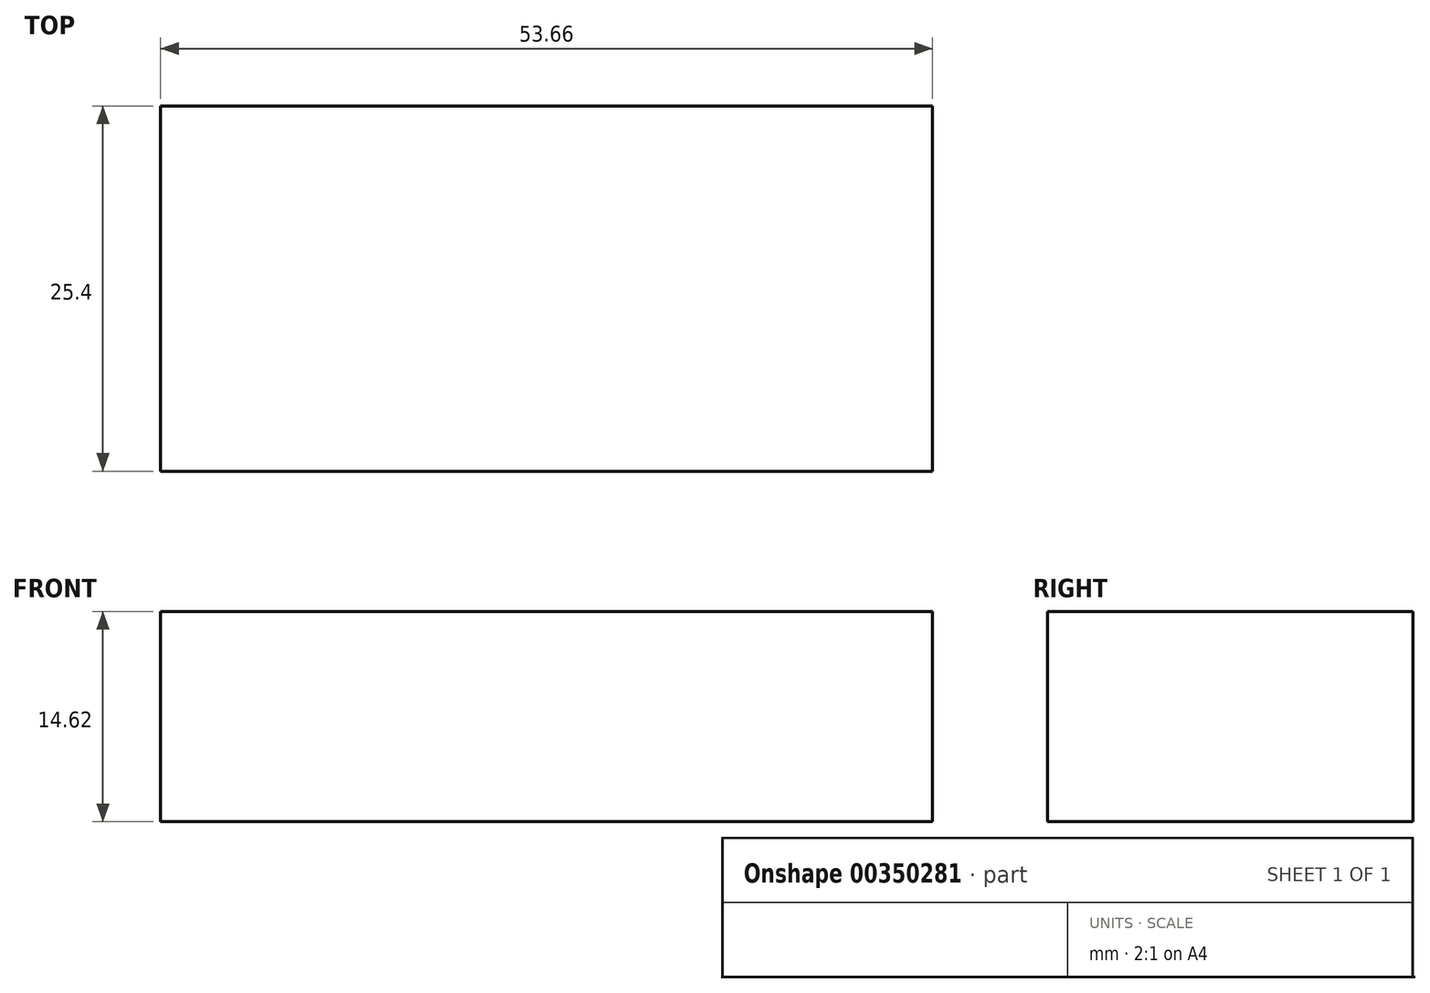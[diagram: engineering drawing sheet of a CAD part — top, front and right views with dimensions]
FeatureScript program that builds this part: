
annotation { "Feature Type Name" : "Feature", "Feature Type Description" : "" }
export const myFeature = defineFeature(function(context is Context, id is Id, definition is map)
    precondition{}
    {
        {
            var Q0;
            Q0=qCreatedBy(makeId("Front.planeOp"),FACE);
            var sketch = newSketch(context, id + "F0", { "sketchPlane" : qUnion([Q0])});
            skLineSegment(sketch, "E0.bottom", {"start": v(0, 0) * mm, "end": v(53.66, 0) * mm});
            skLineSegment(sketch, "E0.top", {"start": v(0, 14.62) * mm, "end": v(53.66, 14.62) * mm});
            skLineSegment(sketch, "E0.left", {"start": v(0, 0) * mm, "end": v(0, 14.62) * mm});
            skLineSegment(sketch, "E0.right", {"start": v(53.66, 0) * mm, "end": v(53.66, 14.62) * mm});
            skSolve(sketch);
        }
        {
            var Q0;
            Q0 = qSketchRegion(id + "F0", true);
            extrude(context, id + "F1", {"entities" : qUnion([Q0]), "depth" : 25.4 * mm});
        }
    });
